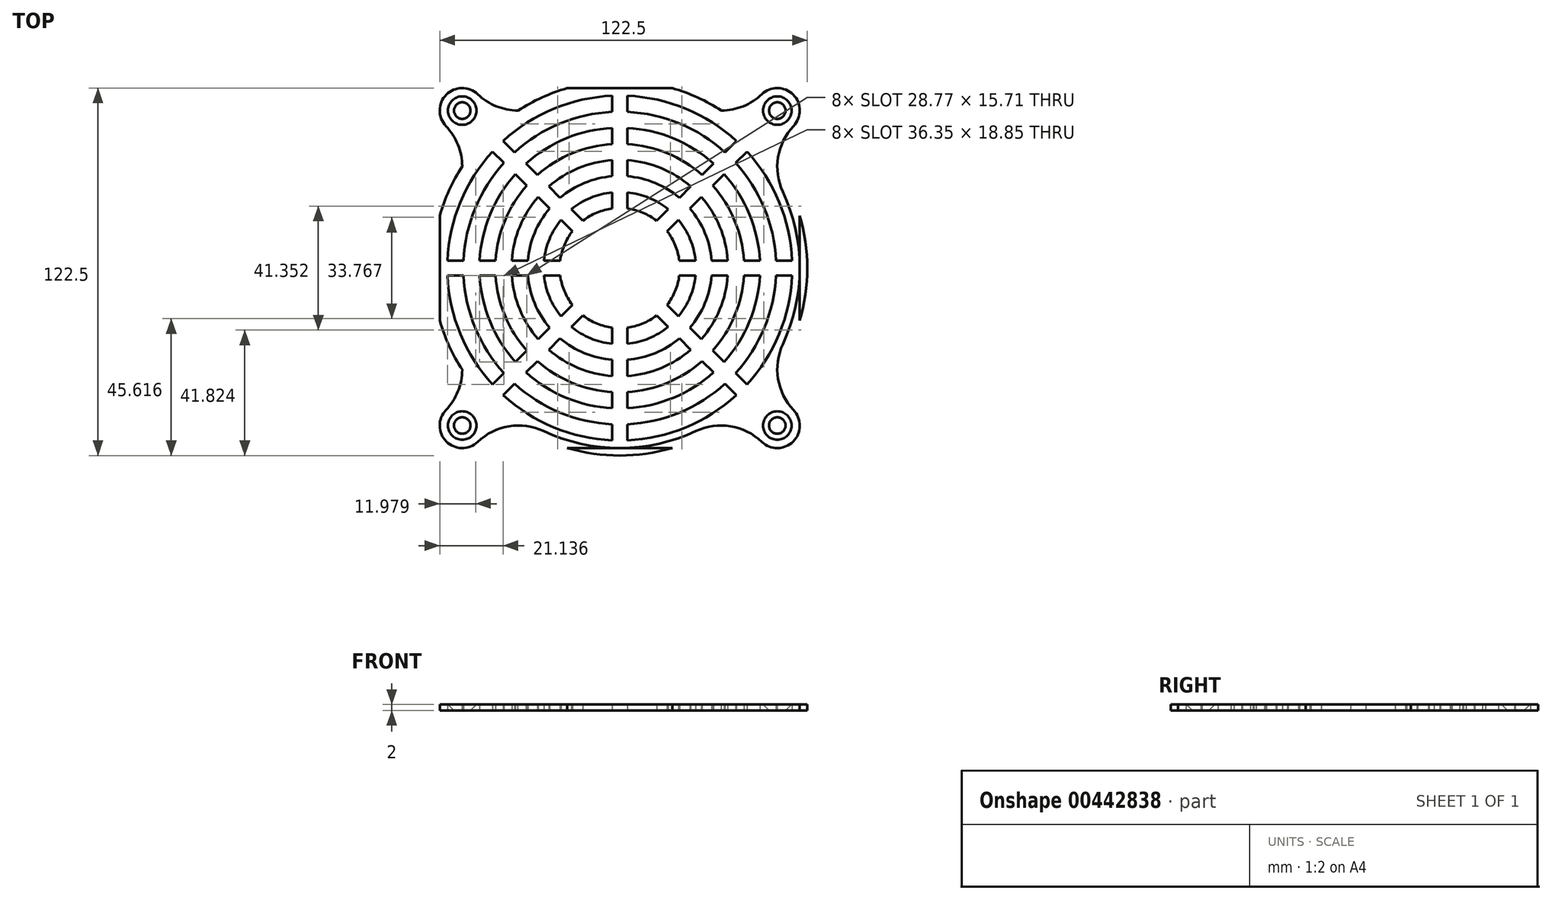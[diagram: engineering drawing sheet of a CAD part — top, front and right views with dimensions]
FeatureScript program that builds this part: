
annotation { "Feature Type Name" : "Feature", "Feature Type Description" : "" }
export const myFeature = defineFeature(function(context is Context, id is Id, definition is map)
    precondition{}
    {
        {
            var Q0;
            Q0=qCreatedBy(makeId("Top.planeOp"),FACE);
            var sketch = newSketch(context, id + "F0", { "sketchPlane" : qUnion([Q0])});
            skCircle(sketch, "E0", {"center": v(-52.5, 52.5) * mm, "radius": 2.75 * mm});
            skLineSegment(sketch, "E1", {"start": v(-52.5, 52.5) * mm, "end": v(52.5, 52.5) * mm, "construction": true});
            skLineSegment(sketch, "E2", {"start": v(52.5, 52.5) * mm, "end": v(52.5, -52.5) * mm, "construction": true});
            skLineSegment(sketch, "E3", {"start": v(52.5, -52.5) * mm, "end": v(-52.5, -52.5) * mm, "construction": true});
            skLineSegment(sketch, "E4", {"start": v(-52.5, -52.5) * mm, "end": v(-52.5, 52.5) * mm, "construction": true});
            skCircle(sketch, "E5", {"center": v(52.5, 52.5) * mm, "radius": 2.75 * mm});
            skCircle(sketch, "E6", {"center": v(52.5, -52.5) * mm, "radius": 2.75 * mm});
            skCircle(sketch, "E7", {"center": v(-52.5, -52.5) * mm, "radius": 2.75 * mm});
            skArc(sketch, "E8", {"start": v(47.33, 57.93) * mm, "mid": v(47.2, 47.2) * mm, "end": v(57.93, 47.33) * mm, "construction": true});
            skArc(sketch, "E9", {"start": v(57.93, 47.33) * mm, "mid": v(57.8, 57.8) * mm, "end": v(47.33, 57.93) * mm});
            skArc(sketch, "E10", {"start": v(-47.33, 57.93) * mm, "mid": v(-57.8, 57.8) * mm, "end": v(-57.93, 47.33) * mm});
            skArc(sketch, "E11", {"start": v(-57.93, 47.33) * mm, "mid": v(-47.2, 47.2) * mm, "end": v(-47.33, 57.93) * mm, "construction": true});
            skArc(sketch, "E12", {"start": v(-57.93, -47.33) * mm, "mid": v(-57.8, -57.8) * mm, "end": v(-47.33, -57.93) * mm});
            skArc(sketch, "E13", {"start": v(-47.33, -57.93) * mm, "mid": v(-47.2, -47.2) * mm, "end": v(-57.93, -47.33) * mm, "construction": true});
            skArc(sketch, "E14", {"start": v(47.33, -57.93) * mm, "mid": v(57.8, -57.8) * mm, "end": v(57.93, -47.33) * mm});
            skArc(sketch, "E15", {"start": v(57.93, -47.33) * mm, "mid": v(47.2, -47.2) * mm, "end": v(47.33, -57.93) * mm, "construction": true});
            skLineSegment(sketch, "E16", {"start": v(-47.33, -57.93) * mm, "end": v(47.33, -57.93) * mm, "construction": true});
            skLineSegment(sketch, "E17", {"start": v(57.93, -47.33) * mm, "end": v(57.93, 47.33) * mm, "construction": true});
            skLineSegment(sketch, "E18", {"start": v(47.33, 57.93) * mm, "end": v(-47.33, 57.93) * mm, "construction": true});
            skLineSegment(sketch, "E19", {"start": v(-57.93, 47.33) * mm, "end": v(-57.93, -47.33) * mm, "construction": true});
            skArc(sketch, "E20", {"start": v(-54.35, 25.41) * mm, "mid": v(-52.76, 36.92) * mm, "end": v(-57.93, 47.33) * mm});
            skArc(sketch, "E21", {"start": v(-47.33, 57.93) * mm, "mid": v(-36.92, 52.76) * mm, "end": v(-25.41, 54.35) * mm});
            skArc(sketch, "E22", {"start": v(25.41, 54.35) * mm, "mid": v(36.92, 52.76) * mm, "end": v(47.33, 57.93) * mm});
            skArc(sketch, "E23", {"start": v(57.93, 47.33) * mm, "mid": v(52.76, 36.92) * mm, "end": v(54.35, 25.41) * mm});
            skArc(sketch, "E24", {"start": v(-57.93, -47.33) * mm, "mid": v(-52.76, -36.92) * mm, "end": v(-54.35, -25.41) * mm});
            skArc(sketch, "E25", {"start": v(-25.41, -54.35) * mm, "mid": v(-36.92, -52.76) * mm, "end": v(-47.33, -57.93) * mm});
            skArc(sketch, "E26", {"start": v(47.33, -57.93) * mm, "mid": v(36.92, -52.76) * mm, "end": v(25.41, -54.35) * mm});
            skArc(sketch, "E27", {"start": v(54.35, -25.41) * mm, "mid": v(52.76, -36.92) * mm, "end": v(57.93, -47.33) * mm});
            skArc(sketch, "E28", {"start": v(-57.45, -2.5) * mm, "mid": v(-40.66, -40.66) * mm, "end": v(-2.5, -57.45) * mm});
            skArc(sketch, "E29", {"start": v(-54.35, 25.41) * mm, "mid": v(-60, 0) * mm, "end": v(-54.35, -25.41) * mm});
            skArc(sketch, "E30", {"start": v(-25.41, 54.35) * mm, "mid": v(-42.43, 42.43) * mm, "end": v(-54.35, 25.41) * mm, "construction": true});
            skArc(sketch, "E31", {"start": v(25.41, 54.35) * mm, "mid": v(0, 60) * mm, "end": v(-25.41, 54.35) * mm});
            skArc(sketch, "E32", {"start": v(54.35, 25.41) * mm, "mid": v(42.43, 42.43) * mm, "end": v(25.41, 54.35) * mm, "construction": true});
            skArc(sketch, "E33", {"start": v(54.35, -25.41) * mm, "mid": v(60, 0) * mm, "end": v(54.35, 25.41) * mm});
            skArc(sketch, "E34", {"start": v(25.41, -54.35) * mm, "mid": v(42.43, -42.43) * mm, "end": v(54.35, -25.41) * mm, "construction": true});
            skArc(sketch, "E35", {"start": v(-25.41, -54.35) * mm, "mid": v(0, -60) * mm, "end": v(25.41, -54.35) * mm});
            skArc(sketch, "E36", {"start": v(-54.35, -25.41) * mm, "mid": v(-42.43, -42.43) * mm, "end": v(-25.41, -54.35) * mm, "construction": true});
            skArc(sketch, "E37.0", {"start": v(-52.08, -2.5) * mm, "mid": v(-36.87, -36.87) * mm, "end": v(-2.5, -52.08) * mm});
            skArc(sketch, "E38.0", {"start": v(-46.72, -2.5) * mm, "mid": v(-33.08, -33.08) * mm, "end": v(-2.5, -46.72) * mm});
            skArc(sketch, "E39.0", {"start": v(-41.35, -2.5) * mm, "mid": v(-29.3, -29.3) * mm, "end": v(-2.5, -41.35) * mm});
            skArc(sketch, "E40.0", {"start": v(-35.98, -2.5) * mm, "mid": v(-25.5, -25.5) * mm, "end": v(-2.5, -35.98) * mm});
            skArc(sketch, "E41.0", {"start": v(-30.61, -2.5) * mm, "mid": v(-21.72, -21.72) * mm, "end": v(-2.5, -30.61) * mm});
            skArc(sketch, "E42.0", {"start": v(-25.23, -2.5) * mm, "mid": v(-17.93, -17.93) * mm, "end": v(-2.5, -25.23) * mm});
            skArc(sketch, "E43", {"start": v(-19.84, -2.5) * mm, "mid": v(-14.14, -14.14) * mm, "end": v(-2.5, -19.84) * mm});
            skLineSegment(sketch, "E44", {"start": v(-46.79, 0) * mm, "end": v(-41.43, 0) * mm, "construction": true});
            skLineSegment(sketch, "E45", {"start": v(-41.43, 0) * mm, "end": v(-36.07, 0) * mm, "construction": true});
            skLineSegment(sketch, "E46", {"start": v(-36.07, 0) * mm, "end": v(-30.71, 0) * mm, "construction": true});
            skLineSegment(sketch, "E47", {"start": v(-30.71, 0) * mm, "end": v(-25.36, 0) * mm, "construction": true});
            skLineSegment(sketch, "E48", {"start": v(-25.36, 0) * mm, "end": v(-20, 0) * mm, "construction": true});
            skLineSegment(sketch, "E49", {"start": v(0, 0) * mm, "end": v(-46.79, 0) * mm, "construction": true});
            skLineSegment(sketch, "E50", {"start": v(-46.79, 0) * mm, "end": v(-52.14, 0) * mm, "construction": true});
            skLineSegment(sketch, "E51", {"start": v(-52.14, 0) * mm, "end": v(-57.5, 0) * mm, "construction": true});
            skLineSegment(sketch, "E52.bottom", {"start": v(-59.95, 2.5) * mm, "end": v(59.95, 2.5) * mm, "construction": true});
            skLineSegment(sketch, "E52.top", {"start": v(-59.95, -2.5) * mm, "end": v(59.95, -2.5) * mm, "construction": true});
            skLineSegment(sketch, "E52.left", {"start": v(-59.95, 2.5) * mm, "end": v(-59.95, -2.5) * mm, "construction": true});
            skLineSegment(sketch, "E52.right", {"start": v(59.95, 2.5) * mm, "end": v(59.95, -2.5) * mm, "construction": true});
            skLineSegment(sketch, "E53.bottom", {"start": v(-2.5, 59.95) * mm, "end": v(2.5, 59.95) * mm, "construction": true});
            skLineSegment(sketch, "E53.top", {"start": v(-2.5, -59.95) * mm, "end": v(2.5, -59.95) * mm, "construction": true});
            skLineSegment(sketch, "E53.left", {"start": v(-2.5, 59.95) * mm, "end": v(-2.5, -59.95) * mm, "construction": true});
            skLineSegment(sketch, "E53.right", {"start": v(2.5, 59.95) * mm, "end": v(2.5, -59.95) * mm, "construction": true});
            skLineSegment(sketch, "E54", {"start": v(-57.45, 2.5) * mm, "end": v(-52.08, 2.5) * mm});
            skLineSegment(sketch, "E55", {"start": v(-57.45, -2.5) * mm, "end": v(-52.08, -2.5) * mm});
            skLineSegment(sketch, "E56", {"start": v(-46.72, 2.5) * mm, "end": v(-41.35, 2.5) * mm});
            skLineSegment(sketch, "E57", {"start": v(-46.72, -2.5) * mm, "end": v(-41.35, -2.5) * mm});
            skLineSegment(sketch, "E58", {"start": v(-35.98, 2.5) * mm, "end": v(-30.61, 2.5) * mm});
            skLineSegment(sketch, "E59", {"start": v(-35.98, -2.5) * mm, "end": v(-30.61, -2.5) * mm});
            skLineSegment(sketch, "E60", {"start": v(-25.23, -2.5) * mm, "end": v(-19.84, -2.5) * mm});
            skLineSegment(sketch, "E61", {"start": v(-19.84, 2.5) * mm, "end": v(-25.23, 2.5) * mm});
            skArc(sketch, "E62.trimOffspring", {"start": v(19.84, 2.5) * mm, "mid": v(14.14, 14.14) * mm, "end": v(2.5, 19.84) * mm});
            skArc(sketch, "E63.trimOffspring", {"start": v(25.23, 2.5) * mm, "mid": v(17.93, 17.93) * mm, "end": v(2.5, 25.23) * mm});
            skArc(sketch, "E64.trimOffspring", {"start": v(30.61, 2.5) * mm, "mid": v(21.72, 21.72) * mm, "end": v(2.5, 30.61) * mm});
            skArc(sketch, "E65.trimOffspring", {"start": v(35.98, 2.5) * mm, "mid": v(25.5, 25.5) * mm, "end": v(2.5, 35.98) * mm});
            skArc(sketch, "E66.trimOffspring", {"start": v(41.35, 2.5) * mm, "mid": v(29.3, 29.3) * mm, "end": v(2.5, 41.35) * mm});
            skArc(sketch, "E67.trimOffspring", {"start": v(46.72, 2.5) * mm, "mid": v(33.08, 33.08) * mm, "end": v(2.5, 46.72) * mm});
            skArc(sketch, "E68.trimOffspring", {"start": v(52.08, 2.5) * mm, "mid": v(36.87, 36.87) * mm, "end": v(2.5, 52.08) * mm});
            skArc(sketch, "E69.trimOffspring", {"start": v(57.45, 2.5) * mm, "mid": v(40.66, 40.66) * mm, "end": v(2.5, 57.45) * mm});
            skLineSegment(sketch, "E70", {"start": v(19.84, 2.5) * mm, "end": v(25.23, 2.5) * mm});
            skLineSegment(sketch, "E71", {"start": v(30.61, 2.5) * mm, "end": v(35.98, 2.5) * mm});
            skLineSegment(sketch, "E72", {"start": v(41.35, 2.5) * mm, "end": v(46.72, 2.5) * mm});
            skLineSegment(sketch, "E73", {"start": v(52.08, 2.5) * mm, "end": v(57.45, 2.5) * mm});
            skLineSegment(sketch, "E74", {"start": v(57.45, -2.5) * mm, "end": v(52.08, -2.5) * mm});
            skLineSegment(sketch, "E75", {"start": v(46.72, -2.5) * mm, "end": v(41.35, -2.5) * mm});
            skLineSegment(sketch, "E76", {"start": v(35.98, -2.5) * mm, "end": v(30.61, -2.5) * mm});
            skLineSegment(sketch, "E77", {"start": v(25.23, -2.5) * mm, "end": v(19.84, -2.5) * mm});
            skArc(sketch, "E78.trimOffspring", {"start": v(-2.5, 19.84) * mm, "mid": v(-14.14, 14.14) * mm, "end": v(-19.84, 2.5) * mm});
            skArc(sketch, "E79.trimOffspring", {"start": v(-2.5, 25.23) * mm, "mid": v(-17.93, 17.93) * mm, "end": v(-25.23, 2.5) * mm});
            skArc(sketch, "E80.trimOffspring", {"start": v(-2.5, 30.61) * mm, "mid": v(-21.72, 21.72) * mm, "end": v(-30.61, 2.5) * mm});
            skArc(sketch, "E81.trimOffspring", {"start": v(-2.5, 35.98) * mm, "mid": v(-25.5, 25.5) * mm, "end": v(-35.98, 2.5) * mm});
            skArc(sketch, "E82.trimOffspring", {"start": v(-2.5, 41.35) * mm, "mid": v(-29.3, 29.3) * mm, "end": v(-41.35, 2.5) * mm});
            skArc(sketch, "E83.trimOffspring", {"start": v(-2.5, 46.72) * mm, "mid": v(-33.08, 33.08) * mm, "end": v(-46.72, 2.5) * mm});
            skArc(sketch, "E84.trimOffspring", {"start": v(-2.5, 57.45) * mm, "mid": v(-40.66, 40.66) * mm, "end": v(-57.45, 2.5) * mm});
            skArc(sketch, "E85.trimOffspring", {"start": v(-2.5, 52.08) * mm, "mid": v(-36.87, 36.87) * mm, "end": v(-52.08, 2.5) * mm});
            skLineSegment(sketch, "E86", {"start": v(-2.5, 19.84) * mm, "end": v(-2.5, 25.23) * mm});
            skLineSegment(sketch, "E87", {"start": v(-2.5, 30.61) * mm, "end": v(-2.5, 35.98) * mm});
            skLineSegment(sketch, "E88", {"start": v(-2.5, 41.35) * mm, "end": v(-2.5, 46.72) * mm});
            skLineSegment(sketch, "E89", {"start": v(-2.5, 52.08) * mm, "end": v(-2.5, 57.45) * mm});
            skLineSegment(sketch, "E90", {"start": v(2.5, 52.08) * mm, "end": v(2.5, 57.45) * mm});
            skLineSegment(sketch, "E91", {"start": v(2.5, 46.72) * mm, "end": v(2.5, 41.35) * mm});
            skLineSegment(sketch, "E92", {"start": v(2.5, 35.98) * mm, "end": v(2.5, 30.61) * mm});
            skLineSegment(sketch, "E93", {"start": v(2.5, 25.23) * mm, "end": v(2.5, 19.84) * mm});
            skArc(sketch, "E94.trimOffspring", {"start": v(2.5, -57.45) * mm, "mid": v(40.66, -40.66) * mm, "end": v(57.45, -2.5) * mm});
            skArc(sketch, "E95.trimOffspring", {"start": v(2.5, -52.08) * mm, "mid": v(36.87, -36.87) * mm, "end": v(52.08, -2.5) * mm});
            skArc(sketch, "E96.trimOffspring", {"start": v(2.5, -46.72) * mm, "mid": v(33.08, -33.08) * mm, "end": v(46.72, -2.5) * mm});
            skArc(sketch, "E97.trimOffspring", {"start": v(2.5, -41.35) * mm, "mid": v(29.3, -29.3) * mm, "end": v(41.35, -2.5) * mm});
            skArc(sketch, "E98.trimOffspring", {"start": v(2.5, -35.98) * mm, "mid": v(25.5, -25.5) * mm, "end": v(35.98, -2.5) * mm});
            skArc(sketch, "E99.trimOffspring", {"start": v(2.5, -30.61) * mm, "mid": v(21.72, -21.72) * mm, "end": v(30.61, -2.5) * mm});
            skArc(sketch, "E100.trimOffspring", {"start": v(2.5, -25.23) * mm, "mid": v(17.93, -17.93) * mm, "end": v(25.23, -2.5) * mm});
            skArc(sketch, "E101.trimOffspring", {"start": v(2.5, -19.84) * mm, "mid": v(14.14, -14.14) * mm, "end": v(19.84, -2.5) * mm});
            skLineSegment(sketch, "E102", {"start": v(-2.5, -19.84) * mm, "end": v(-2.5, -25.23) * mm});
            skLineSegment(sketch, "E103", {"start": v(-2.5, -30.61) * mm, "end": v(-2.5, -35.98) * mm});
            skLineSegment(sketch, "E104", {"start": v(-2.5, -41.35) * mm, "end": v(-2.5, -46.72) * mm});
            skLineSegment(sketch, "E105", {"start": v(-2.5, -52.08) * mm, "end": v(-2.5, -57.45) * mm});
            skLineSegment(sketch, "E106", {"start": v(2.5, -57.45) * mm, "end": v(2.5, -52.08) * mm});
            skLineSegment(sketch, "E107", {"start": v(2.5, -46.72) * mm, "end": v(2.5, -41.35) * mm});
            skLineSegment(sketch, "E108", {"start": v(2.5, -35.98) * mm, "end": v(2.5, -30.61) * mm});
            skLineSegment(sketch, "E109", {"start": v(2.5, -25.23) * mm, "end": v(2.5, -19.84) * mm});
            skLineSegment(sketch, "E110", {"start": v(-57.8, 57.8) * mm, "end": v(0, 0) * mm, "construction": true});
            skSolve(sketch);
        }
        {
            var Q0;
            Q0=makeQuery(id+"F0.imprint","IMPRINT",FACE,{"disambiguationData":[TD([[makeQuery(id+"F0.imprint","IMPRINT",EDGE,{"derivedFrom":sQuery(id+"F0.wireOp",EDGE,"E0")}),-1.0]])]});
            extrude(context, id + "F1", {"entities" : qUnion([Q0]), "depth" : 2 * mm});
        }
        {
            var Q0;
            Q0=makeQuery(id+"F1.opExtrude","CAP_EDGE",EDGE,{"disambiguationData":[OSD([sQuery(id+"F0.wireOp",EDGE,"E7")])],"isStart":false});
            var Q1;
            Q1=makeQuery(id+"F1.opExtrude","CAP_EDGE",EDGE,{"disambiguationData":[OSD([sQuery(id+"F0.wireOp",EDGE,"E0")])],"isStart":false});
            var Q2;
            Q2=makeQuery(id+"F1.opExtrude","CAP_EDGE",EDGE,{"disambiguationData":[OSD([sQuery(id+"F0.wireOp",EDGE,"E5")])],"isStart":false});
            var Q3;
            Q3=makeQuery(id+"F1.opExtrude","CAP_EDGE",EDGE,{"disambiguationData":[OSD([sQuery(id+"F0.wireOp",EDGE,"E6")])],"isStart":false});
            chamfer(context, id + "F2", {"entities" : qUnion([Q0, Q1, Q2, Q3]), "width" : 2 * mm, "tangentPropagation" : true});
        }
        {
            var Q0;
            Q0=makeQuery(id+"F1.opExtrude","CAP_FACE",FACE,{"disambiguationData":[OSD([sQuery(id+"F0.wireOp",EDGE,"E0"),sQuery(id+"F0.wireOp",EDGE,"E5"),sQuery(id+"F0.wireOp",EDGE,"E6"),sQuery(id+"F0.wireOp",EDGE,"E7"),sQuery(id+"F0.wireOp",EDGE,"E9"),sQuery(id+"F0.wireOp",EDGE,"E10"),sQuery(id+"F0.wireOp",EDGE,"E12"),sQuery(id+"F0.wireOp",EDGE,"E14"),sQuery(id+"F0.wireOp",EDGE,"E20"),sQuery(id+"F0.wireOp",EDGE,"E21"),sQuery(id+"F0.wireOp",EDGE,"E22"),sQuery(id+"F0.wireOp",EDGE,"E23"),sQuery(id+"F0.wireOp",EDGE,"E24"),sQuery(id+"F0.wireOp",EDGE,"E25"),sQuery(id+"F0.wireOp",EDGE,"E26"),sQuery(id+"F0.wireOp",EDGE,"E27"),sQuery(id+"F0.wireOp",EDGE,"E28"),sQuery(id+"F0.wireOp",EDGE,"E29"),sQuery(id+"F0.wireOp",EDGE,"E31"),sQuery(id+"F0.wireOp",EDGE,"E33"),sQuery(id+"F0.wireOp",EDGE,"E35"),sQuery(id+"F0.wireOp",EDGE,"E37.0"),sQuery(id+"F0.wireOp",EDGE,"E38.0"),sQuery(id+"F0.wireOp",EDGE,"E39.0"),sQuery(id+"F0.wireOp",EDGE,"E40.0"),sQuery(id+"F0.wireOp",EDGE,"E41.0"),sQuery(id+"F0.wireOp",EDGE,"E42.0"),sQuery(id+"F0.wireOp",EDGE,"E43"),sQuery(id+"F0.wireOp",EDGE,"E54"),sQuery(id+"F0.wireOp",EDGE,"E55"),sQuery(id+"F0.wireOp",EDGE,"E56"),sQuery(id+"F0.wireOp",EDGE,"E57"),sQuery(id+"F0.wireOp",EDGE,"E58"),sQuery(id+"F0.wireOp",EDGE,"E59"),sQuery(id+"F0.wireOp",EDGE,"E60"),sQuery(id+"F0.wireOp",EDGE,"E61"),sQuery(id+"F0.wireOp",EDGE,"E62.trimOffspring"),sQuery(id+"F0.wireOp",EDGE,"E63.trimOffspring"),sQuery(id+"F0.wireOp",EDGE,"E64.trimOffspring"),sQuery(id+"F0.wireOp",EDGE,"E65.trimOffspring"),sQuery(id+"F0.wireOp",EDGE,"E66.trimOffspring"),sQuery(id+"F0.wireOp",EDGE,"E67.trimOffspring"),sQuery(id+"F0.wireOp",EDGE,"E68.trimOffspring"),sQuery(id+"F0.wireOp",EDGE,"E69.trimOffspring"),sQuery(id+"F0.wireOp",EDGE,"E70"),sQuery(id+"F0.wireOp",EDGE,"E71"),sQuery(id+"F0.wireOp",EDGE,"E72"),sQuery(id+"F0.wireOp",EDGE,"E73"),sQuery(id+"F0.wireOp",EDGE,"E74"),sQuery(id+"F0.wireOp",EDGE,"E75"),sQuery(id+"F0.wireOp",EDGE,"E76"),sQuery(id+"F0.wireOp",EDGE,"E77"),sQuery(id+"F0.wireOp",EDGE,"E78.trimOffspring"),sQuery(id+"F0.wireOp",EDGE,"E79.trimOffspring"),sQuery(id+"F0.wireOp",EDGE,"E80.trimOffspring"),sQuery(id+"F0.wireOp",EDGE,"E81.trimOffspring"),sQuery(id+"F0.wireOp",EDGE,"E82.trimOffspring"),sQuery(id+"F0.wireOp",EDGE,"E83.trimOffspring"),sQuery(id+"F0.wireOp",EDGE,"E84.trimOffspring"),sQuery(id+"F0.wireOp",EDGE,"E85.trimOffspring"),sQuery(id+"F0.wireOp",EDGE,"E86"),sQuery(id+"F0.wireOp",EDGE,"E87"),sQuery(id+"F0.wireOp",EDGE,"E88"),sQuery(id+"F0.wireOp",EDGE,"E89"),sQuery(id+"F0.wireOp",EDGE,"E90"),sQuery(id+"F0.wireOp",EDGE,"E91"),sQuery(id+"F0.wireOp",EDGE,"E92"),sQuery(id+"F0.wireOp",EDGE,"E93"),sQuery(id+"F0.wireOp",EDGE,"E94.trimOffspring"),sQuery(id+"F0.wireOp",EDGE,"E95.trimOffspring"),sQuery(id+"F0.wireOp",EDGE,"E96.trimOffspring"),sQuery(id+"F0.wireOp",EDGE,"E97.trimOffspring"),sQuery(id+"F0.wireOp",EDGE,"E98.trimOffspring"),sQuery(id+"F0.wireOp",EDGE,"E99.trimOffspring"),sQuery(id+"F0.wireOp",EDGE,"E100.trimOffspring"),sQuery(id+"F0.wireOp",EDGE,"E101.trimOffspring"),sQuery(id+"F0.wireOp",EDGE,"E102"),sQuery(id+"F0.wireOp",EDGE,"E103"),sQuery(id+"F0.wireOp",EDGE,"E104"),sQuery(id+"F0.wireOp",EDGE,"E105"),sQuery(id+"F0.wireOp",EDGE,"E106"),sQuery(id+"F0.wireOp",EDGE,"E107"),sQuery(id+"F0.wireOp",EDGE,"E108"),sQuery(id+"F0.wireOp",EDGE,"E109")])],"isStart":false});
            var sketch = newSketch(context, id + "F3", { "sketchPlane" : qUnion([Q0])});
            skLineSegment(sketch, "E111", {"start": v(-47.66, 44.12) * mm, "end": v(44.12, -47.66) * mm});
            skLineSegment(sketch, "E112", {"start": v(44.12, -47.66) * mm, "end": v(47.66, -44.12) * mm});
            skLineSegment(sketch, "E113", {"start": v(47.66, -44.12) * mm, "end": v(-44.12, 47.66) * mm});
            skLineSegment(sketch, "E114", {"start": v(-44.12, 47.66) * mm, "end": v(-47.66, 44.12) * mm});
            skLineSegment(sketch, "E115", {"start": v(-47.66, 44.12) * mm, "end": v(47.66, -44.12) * mm, "construction": true});
            skLineSegment(sketch, "E116.1.0", {"start": v(-44.12, -47.66) * mm, "end": v(47.66, 44.12) * mm});
            skLineSegment(sketch, "E116.1.1", {"start": v(44.12, 47.66) * mm, "end": v(-47.66, -44.12) * mm});
            skLineSegment(sketch, "E116.1.2", {"start": v(-47.66, -44.12) * mm, "end": v(-44.12, -47.66) * mm});
            skLineSegment(sketch, "E116.1.3", {"start": v(47.66, 44.12) * mm, "end": v(44.12, 47.66) * mm});
            skLineSegment(sketch, "E116.3.0", {"start": v(44.12, 47.66) * mm, "end": v(-47.66, -44.12) * mm});
            skLineSegment(sketch, "E116.3.1", {"start": v(-44.12, -47.66) * mm, "end": v(47.66, 44.12) * mm});
            skLineSegment(sketch, "E116.3.2", {"start": v(47.66, 44.12) * mm, "end": v(44.12, 47.66) * mm});
            skLineSegment(sketch, "E116.3.3", {"start": v(-47.66, -44.12) * mm, "end": v(-44.12, -47.66) * mm});
            skPoint(sketch, "E116.center", {"position": v(0, 0) * mm});
            skSolve(sketch);
        }
        {
            var Q0;
            Q0 = qSketchRegion(id + "F3", true);
            extrude(context, id + "F4", {"entities" : qUnion([Q0]), "operationType" : NewBodyOperationType.ADD, "oppositeDirection" : true, "depth" : 2 * mm, "offsetDistance" : 25 * mm});
        }
        {
            var Q0;
            Q0=makeQuery(id+"F4.boolean.opBoolean","MERGE",FACE,{"derivedFrom":[makeQuery(id+"F1.opExtrude","CAP_FACE",FACE,{"disambiguationData":[OSD([sQuery(id+"F0.wireOp",EDGE,"E0"),sQuery(id+"F0.wireOp",EDGE,"E5"),sQuery(id+"F0.wireOp",EDGE,"E6"),sQuery(id+"F0.wireOp",EDGE,"E7"),sQuery(id+"F0.wireOp",EDGE,"E9"),sQuery(id+"F0.wireOp",EDGE,"E10"),sQuery(id+"F0.wireOp",EDGE,"E12"),sQuery(id+"F0.wireOp",EDGE,"E14"),sQuery(id+"F0.wireOp",EDGE,"E20"),sQuery(id+"F0.wireOp",EDGE,"E21"),sQuery(id+"F0.wireOp",EDGE,"E22"),sQuery(id+"F0.wireOp",EDGE,"E23"),sQuery(id+"F0.wireOp",EDGE,"E24"),sQuery(id+"F0.wireOp",EDGE,"E25"),sQuery(id+"F0.wireOp",EDGE,"E26"),sQuery(id+"F0.wireOp",EDGE,"E27"),sQuery(id+"F0.wireOp",EDGE,"E28"),sQuery(id+"F0.wireOp",EDGE,"E29"),sQuery(id+"F0.wireOp",EDGE,"E31"),sQuery(id+"F0.wireOp",EDGE,"E33"),sQuery(id+"F0.wireOp",EDGE,"E35"),sQuery(id+"F0.wireOp",EDGE,"E37.0"),sQuery(id+"F0.wireOp",EDGE,"E38.0"),sQuery(id+"F0.wireOp",EDGE,"E39.0"),sQuery(id+"F0.wireOp",EDGE,"E40.0"),sQuery(id+"F0.wireOp",EDGE,"E41.0"),sQuery(id+"F0.wireOp",EDGE,"E42.0"),sQuery(id+"F0.wireOp",EDGE,"E43"),sQuery(id+"F0.wireOp",EDGE,"E54"),sQuery(id+"F0.wireOp",EDGE,"E55"),sQuery(id+"F0.wireOp",EDGE,"E56"),sQuery(id+"F0.wireOp",EDGE,"E57"),sQuery(id+"F0.wireOp",EDGE,"E58"),sQuery(id+"F0.wireOp",EDGE,"E59"),sQuery(id+"F0.wireOp",EDGE,"E60"),sQuery(id+"F0.wireOp",EDGE,"E61"),sQuery(id+"F0.wireOp",EDGE,"E62.trimOffspring"),sQuery(id+"F0.wireOp",EDGE,"E63.trimOffspring"),sQuery(id+"F0.wireOp",EDGE,"E64.trimOffspring"),sQuery(id+"F0.wireOp",EDGE,"E65.trimOffspring"),sQuery(id+"F0.wireOp",EDGE,"E66.trimOffspring"),sQuery(id+"F0.wireOp",EDGE,"E67.trimOffspring"),sQuery(id+"F0.wireOp",EDGE,"E68.trimOffspring"),sQuery(id+"F0.wireOp",EDGE,"E69.trimOffspring"),sQuery(id+"F0.wireOp",EDGE,"E70"),sQuery(id+"F0.wireOp",EDGE,"E71"),sQuery(id+"F0.wireOp",EDGE,"E72"),sQuery(id+"F0.wireOp",EDGE,"E73"),sQuery(id+"F0.wireOp",EDGE,"E74"),sQuery(id+"F0.wireOp",EDGE,"E75"),sQuery(id+"F0.wireOp",EDGE,"E76"),sQuery(id+"F0.wireOp",EDGE,"E77"),sQuery(id+"F0.wireOp",EDGE,"E78.trimOffspring"),sQuery(id+"F0.wireOp",EDGE,"E79.trimOffspring"),sQuery(id+"F0.wireOp",EDGE,"E80.trimOffspring"),sQuery(id+"F0.wireOp",EDGE,"E81.trimOffspring"),sQuery(id+"F0.wireOp",EDGE,"E82.trimOffspring"),sQuery(id+"F0.wireOp",EDGE,"E83.trimOffspring"),sQuery(id+"F0.wireOp",EDGE,"E84.trimOffspring"),sQuery(id+"F0.wireOp",EDGE,"E85.trimOffspring"),sQuery(id+"F0.wireOp",EDGE,"E86"),sQuery(id+"F0.wireOp",EDGE,"E87"),sQuery(id+"F0.wireOp",EDGE,"E88"),sQuery(id+"F0.wireOp",EDGE,"E89"),sQuery(id+"F0.wireOp",EDGE,"E90"),sQuery(id+"F0.wireOp",EDGE,"E91"),sQuery(id+"F0.wireOp",EDGE,"E92"),sQuery(id+"F0.wireOp",EDGE,"E93"),sQuery(id+"F0.wireOp",EDGE,"E94.trimOffspring"),sQuery(id+"F0.wireOp",EDGE,"E95.trimOffspring"),sQuery(id+"F0.wireOp",EDGE,"E96.trimOffspring"),sQuery(id+"F0.wireOp",EDGE,"E97.trimOffspring"),sQuery(id+"F0.wireOp",EDGE,"E98.trimOffspring"),sQuery(id+"F0.wireOp",EDGE,"E99.trimOffspring"),sQuery(id+"F0.wireOp",EDGE,"E100.trimOffspring"),sQuery(id+"F0.wireOp",EDGE,"E101.trimOffspring"),sQuery(id+"F0.wireOp",EDGE,"E102"),sQuery(id+"F0.wireOp",EDGE,"E103"),sQuery(id+"F0.wireOp",EDGE,"E104"),sQuery(id+"F0.wireOp",EDGE,"E105"),sQuery(id+"F0.wireOp",EDGE,"E106"),sQuery(id+"F0.wireOp",EDGE,"E107"),sQuery(id+"F0.wireOp",EDGE,"E108"),sQuery(id+"F0.wireOp",EDGE,"E109")])],"isStart":false}),makeQuery(id+"F4.opExtrude","CAP_FACE",FACE,{"disambiguationData":[OSD([sQuery(id+"F3.wireOp",EDGE,"E113"),sQuery(id+"F3.wireOp",EDGE,"E111"),sQuery(id+"F3.wireOp",EDGE,"E112"),sQuery(id+"F3.wireOp",EDGE,"E114"),sQuery(id+"F3.wireOp",EDGE,"E116.3.0"),sQuery(id+"F3.wireOp",EDGE,"E116.3.1"),sQuery(id+"F3.wireOp",EDGE,"E116.3.2"),sQuery(id+"F3.wireOp",EDGE,"E116.3.3")])],"isStart":true})]});
            var sketch = newSketch(context, id + "F5", { "sketchPlane" : qUnion([Q0])});
            skCircle(sketch, "E117", {"center": v(0, 0) * mm, "radius": 57.5 * mm});
            skCircle(sketch, "E118", {"center": v(0, 0) * mm, "radius": 62.5 * mm});
            skLineSegment(sketch, "E119.bottom", {"start": v(-60, 60) * mm, "end": v(60, 60) * mm});
            skLineSegment(sketch, "E119.top", {"start": v(-60, -60) * mm, "end": v(60, -60) * mm});
            skLineSegment(sketch, "E119.left", {"start": v(-60, 60) * mm, "end": v(-60, -60) * mm});
            skLineSegment(sketch, "E119.right", {"start": v(60, 60) * mm, "end": v(60, -60) * mm});
            skSolve(sketch);
        }
        {
            var Q0;
            {var subQ0=sQuery(id+"F5.wireOp",EDGE,"E119.top");var subQ1=sQuery(id+"F5.wireOp",EDGE,"E118");var subQ2=makeQuery(id+"F5.imprint","INTERSECT",VERTEX,{"disambiguationData":[OD(0.0)],"derivedFrom":[subQ1,subQ0]});Q0=makeQuery(id+"F5.imprint","IMPRINT",FACE,{"disambiguationData":[TD([[makeQuery(id+"F5.imprint","IMPRINT",EDGE,{"disambiguationData":[TD([[subQ2,1.0]])],"derivedFrom":subQ1}),1.0]])]});}
            var Q1;
            {var subQ0=sQuery(id+"F5.wireOp",EDGE,"E119.top");var subQ1=sQuery(id+"F5.wireOp",EDGE,"E118");var subQ2=makeQuery(id+"F5.imprint","INTERSECT",VERTEX,{"disambiguationData":[OD(1.0)],"derivedFrom":[subQ1,subQ0]});Q1=makeQuery(id+"F5.imprint","IMPRINT",FACE,{"disambiguationData":[TD([[makeQuery(id+"F5.imprint","IMPRINT",EDGE,{"disambiguationData":[TD([[subQ2,-1.0]])],"derivedFrom":subQ1}),1.0]])]});}
            var Q2;
            {var subQ0=sQuery(id+"F5.wireOp",EDGE,"E119.left");var subQ1=sQuery(id+"F5.wireOp",EDGE,"E118");var subQ2=makeQuery(id+"F5.imprint","INTERSECT",VERTEX,{"disambiguationData":[OD(1.0)],"derivedFrom":[subQ1,subQ0]});Q2=makeQuery(id+"F5.imprint","IMPRINT",FACE,{"disambiguationData":[TD([[makeQuery(id+"F5.imprint","IMPRINT",EDGE,{"disambiguationData":[TD([[subQ2,-1.0]])],"derivedFrom":subQ1}),1.0]])]});}
            var Q3;
            {var subQ0=sQuery(id+"F5.wireOp",EDGE,"E119.left");var subQ1=sQuery(id+"F5.wireOp",EDGE,"E118");var subQ2=makeQuery(id+"F5.imprint","INTERSECT",VERTEX,{"disambiguationData":[OD(0.0)],"derivedFrom":[subQ1,subQ0]});Q3=makeQuery(id+"F5.imprint","IMPRINT",FACE,{"disambiguationData":[TD([[makeQuery(id+"F5.imprint","IMPRINT",EDGE,{"disambiguationData":[TD([[subQ2,1.0]])],"derivedFrom":subQ1}),1.0]])]});}
            var Q4;
            {var subQ0=sQuery(id+"F5.wireOp",EDGE,"E119.bottom");var subQ1=sQuery(id+"F5.wireOp",EDGE,"E118");var subQ2=makeQuery(id+"F5.imprint","INTERSECT",VERTEX,{"disambiguationData":[OD(1.0)],"derivedFrom":[subQ1,subQ0]});Q4=makeQuery(id+"F5.imprint","IMPRINT",FACE,{"disambiguationData":[TD([[makeQuery(id+"F5.imprint","IMPRINT",EDGE,{"disambiguationData":[TD([[subQ2,-1.0]])],"derivedFrom":subQ1}),1.0]])]});}
            var Q5;
            {var subQ0=sQuery(id+"F5.wireOp",EDGE,"E119.bottom");var subQ1=sQuery(id+"F5.wireOp",EDGE,"E118");var subQ2=makeQuery(id+"F5.imprint","INTERSECT",VERTEX,{"disambiguationData":[OD(0.0)],"derivedFrom":[subQ1,subQ0]});Q5=makeQuery(id+"F5.imprint","IMPRINT",FACE,{"disambiguationData":[TD([[makeQuery(id+"F5.imprint","IMPRINT",EDGE,{"disambiguationData":[TD([[subQ2,1.0]])],"derivedFrom":subQ1}),1.0]])]});}
            var Q6;
            {var subQ0=sQuery(id+"F5.wireOp",EDGE,"E119.right");var subQ1=sQuery(id+"F5.wireOp",EDGE,"E118");var subQ2=makeQuery(id+"F5.imprint","INTERSECT",VERTEX,{"disambiguationData":[OD(0.0)],"derivedFrom":[subQ1,subQ0]});Q6=makeQuery(id+"F5.imprint","IMPRINT",FACE,{"disambiguationData":[TD([[makeQuery(id+"F5.imprint","IMPRINT",EDGE,{"disambiguationData":[TD([[subQ2,-1.0]])],"derivedFrom":subQ1}),1.0]])]});}
            var Q7;
            {var subQ0=sQuery(id+"F5.wireOp",EDGE,"E119.right");var subQ1=sQuery(id+"F5.wireOp",EDGE,"E118");var subQ2=makeQuery(id+"F5.imprint","INTERSECT",VERTEX,{"disambiguationData":[OD(1.0)],"derivedFrom":[subQ1,subQ0]});Q7=makeQuery(id+"F5.imprint","IMPRINT",FACE,{"disambiguationData":[TD([[makeQuery(id+"F5.imprint","IMPRINT",EDGE,{"disambiguationData":[TD([[subQ2,1.0]])],"derivedFrom":subQ1}),1.0]])]});}
            extrude(context, id + "F6", {"entities" : qUnion([Q0, Q1, Q2, Q3, Q4, Q5, Q6, Q7]), "operationType" : NewBodyOperationType.ADD, "oppositeDirection" : true, "depth" : 2 * mm, "offsetDistance" : 25 * mm});
        }
    });
